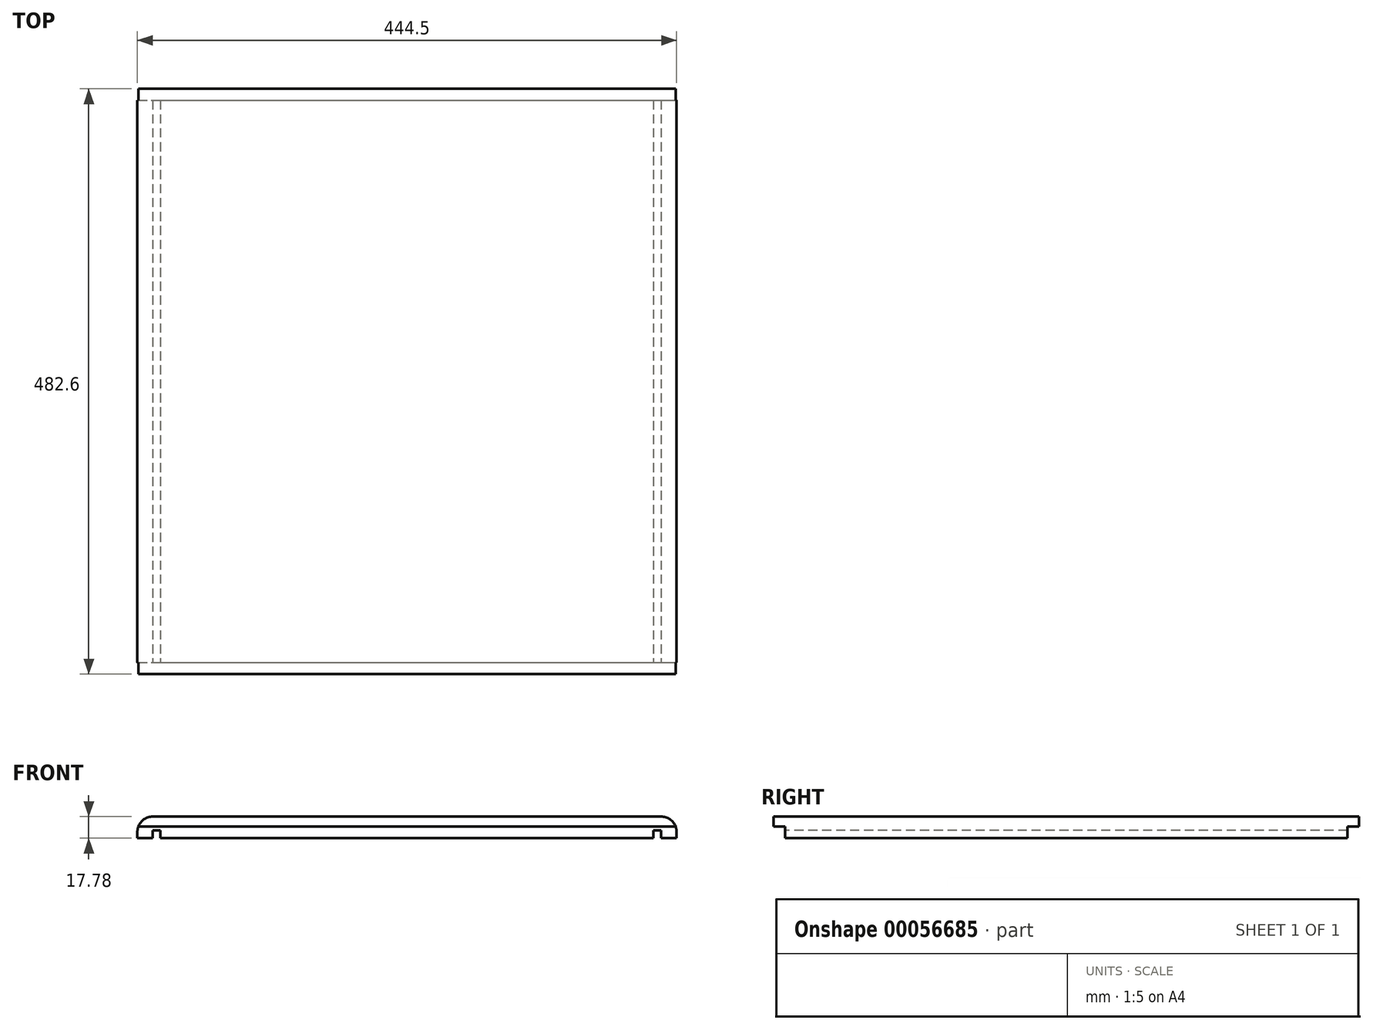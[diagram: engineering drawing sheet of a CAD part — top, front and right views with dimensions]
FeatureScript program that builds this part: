
annotation { "Feature Type Name" : "Feature", "Feature Type Description" : "" }
export const myFeature = defineFeature(function(context is Context, id is Id, definition is map)
    precondition{}
    {
        {
            var Q0;
            Q0=qCreatedBy(makeId("Top.planeOp"),FACE);
            var sketch = newSketch(context, id + "F0", { "sketchPlane" : qUnion([Q0])});
            skLineSegment(sketch, "E0.bottom", {"start": v(-247.52, 241.48) * mm, "end": v(196.98, 241.48) * mm});
            skLineSegment(sketch, "E0.top", {"start": v(-247.52, -241.12) * mm, "end": v(196.98, -241.12) * mm});
            skLineSegment(sketch, "E0.left", {"start": v(-247.52, 241.48) * mm, "end": v(-247.52, -241.12) * mm});
            skLineSegment(sketch, "E0.right", {"start": v(196.98, 241.48) * mm, "end": v(196.98, -241.12) * mm});
            skSolve(sketch);
        }
        {
            var Q0;
            Q0 = qSketchRegion(id + "F0", true);
            var Q1;
            Q1=makeQuery(id+"F0.imprint","IMPRINT",FACE,{"disambiguationData":[TD([[makeQuery(id+"F0.imprint","IMPRINT",EDGE,{"derivedFrom":sQuery(id+"F0.wireOp",EDGE,"E0.bottom")}),-1.0]])]});
            extrude(context, id + "F1", {"entities" : qUnion([Q0, Q1]), "depth" : 17.78 * mm});
        }
        {
            var Q0;
            Q0=makeQuery(id+"F1.opExtrude","SWEPT_FACE",FACE,{"disambiguationData":[OSD([sQuery(id+"F0.wireOp",EDGE,"E0.right")])]});
            var sketch = newSketch(context, id + "F2", { "sketchPlane" : qUnion([Q0])});
            skLineSegment(sketch, "E1.bottom", {"start": v(241.48, 9.53) * mm, "end": v(231.96, 9.53) * mm});
            skLineSegment(sketch, "E1.top", {"start": v(241.48, 0) * mm, "end": v(231.96, 0) * mm});
            skLineSegment(sketch, "E1.left", {"start": v(241.48, 9.53) * mm, "end": v(241.48, 0) * mm});
            skLineSegment(sketch, "E1.right", {"start": v(231.96, 9.52) * mm, "end": v(231.96, 0) * mm});
            skLineSegment(sketch, "E2.bottom", {"start": v(-241.12, 9.53) * mm, "end": v(-231.6, 9.53) * mm});
            skLineSegment(sketch, "E2.top", {"start": v(-241.12, 0) * mm, "end": v(-231.6, 0) * mm});
            skLineSegment(sketch, "E2.left", {"start": v(-241.12, 9.52) * mm, "end": v(-241.12, 0) * mm});
            skLineSegment(sketch, "E2.right", {"start": v(-231.6, 9.53) * mm, "end": v(-231.6, 0) * mm});
            skSolve(sketch);
        }
        {
            var Q0;
            Q0 = qSketchRegion(id + "F2", true);
            extrude(context, id + "F3", {"entities" : qUnion([Q0]), "operationType" : NewBodyOperationType.REMOVE, "oppositeDirection" : true, "depth" : 444.5 * mm});
        }
        {
            var Q0;
            Q0 = qSketchRegion(id + "F2", true);
            extrude(context, id + "F4", {"entities" : qUnion([Q0]), "operationType" : NewBodyOperationType.REMOVE, "oppositeDirection" : true, "depth" : 444.5 * mm});
        }
        {
            var Q0;
            Q0=makeQuery(id+"F1.opExtrude","CAP_FACE",FACE,{"disambiguationData":[OSD([sQuery(id+"F0.wireOp",EDGE,"E0.bottom"),sQuery(id+"F0.wireOp",EDGE,"E0.top"),sQuery(id+"F0.wireOp",EDGE,"E0.left"),sQuery(id+"F0.wireOp",EDGE,"E0.right")])],"isStart":true});
            var sketch = newSketch(context, id + "F5", { "sketchPlane" : qUnion([Q0])});
            skLineSegment(sketch, "E3.bottom", {"start": v(-234.82, -231.96) * mm, "end": v(-228.47, -231.96) * mm});
            skLineSegment(sketch, "E3.top", {"start": v(-234.82, 231.6) * mm, "end": v(-228.47, 231.6) * mm});
            skLineSegment(sketch, "E3.left", {"start": v(-234.82, -231.96) * mm, "end": v(-234.82, 231.6) * mm});
            skLineSegment(sketch, "E3.right", {"start": v(-228.47, -231.96) * mm, "end": v(-228.47, 231.6) * mm});
            skLineSegment(sketch, "E4", {"start": v(-25.27, -231.96) * mm, "end": v(-25.27, 231.6) * mm});
            skLineSegment(sketch, "E5.MirrorCS", {"start": v(184.28, -231.96) * mm, "end": v(184.28, 231.6) * mm});
            skLineSegment(sketch, "E6.MirrorCS", {"start": v(177.93, -231.96) * mm, "end": v(177.93, 231.6) * mm});
            skSolve(sketch);
        }
        {
            var Q0;
            Q0=makeQuery(id+"F1.opExtrude","CAP_EDGE",EDGE,{"disambiguationData":[OSD([sQuery(id+"F0.wireOp",EDGE,"E0.right")])],"isStart":false});
            var Q1;
            Q1=makeQuery(id+"F1.opExtrude","CAP_EDGE",EDGE,{"disambiguationData":[OSD([sQuery(id+"F0.wireOp",EDGE,"E0.left")])],"isStart":false});
            fillet(context, id + "F6", {"entities" : qUnion([Q0, Q1]), "radius" : 12.7 * mm, "tangentPropagation" : true, "allowEdgeOverflow" : false});
        }
        {
            var Q0;
            Q0 = qSketchRegion(id + "F5", true);
            var Q1;
            {var subQ0=sQuery(id+"F5.wireOp",EDGE,"E5.MirrorCS");Q1=makeQuery(id+"F5.imprint","IMPRINT",FACE,{"disambiguationData":[TD([[makeQuery(id+"F5.imprint","IMPRINT",EDGE,{"derivedFrom":subQ0}),1.0]])]});}
            extrude(context, id + "F7", {"entities" : qUnion([Q0, Q1]), "operationType" : NewBodyOperationType.REMOVE, "oppositeDirection" : true, "depth" : 6.35 * mm});
        }
    });
